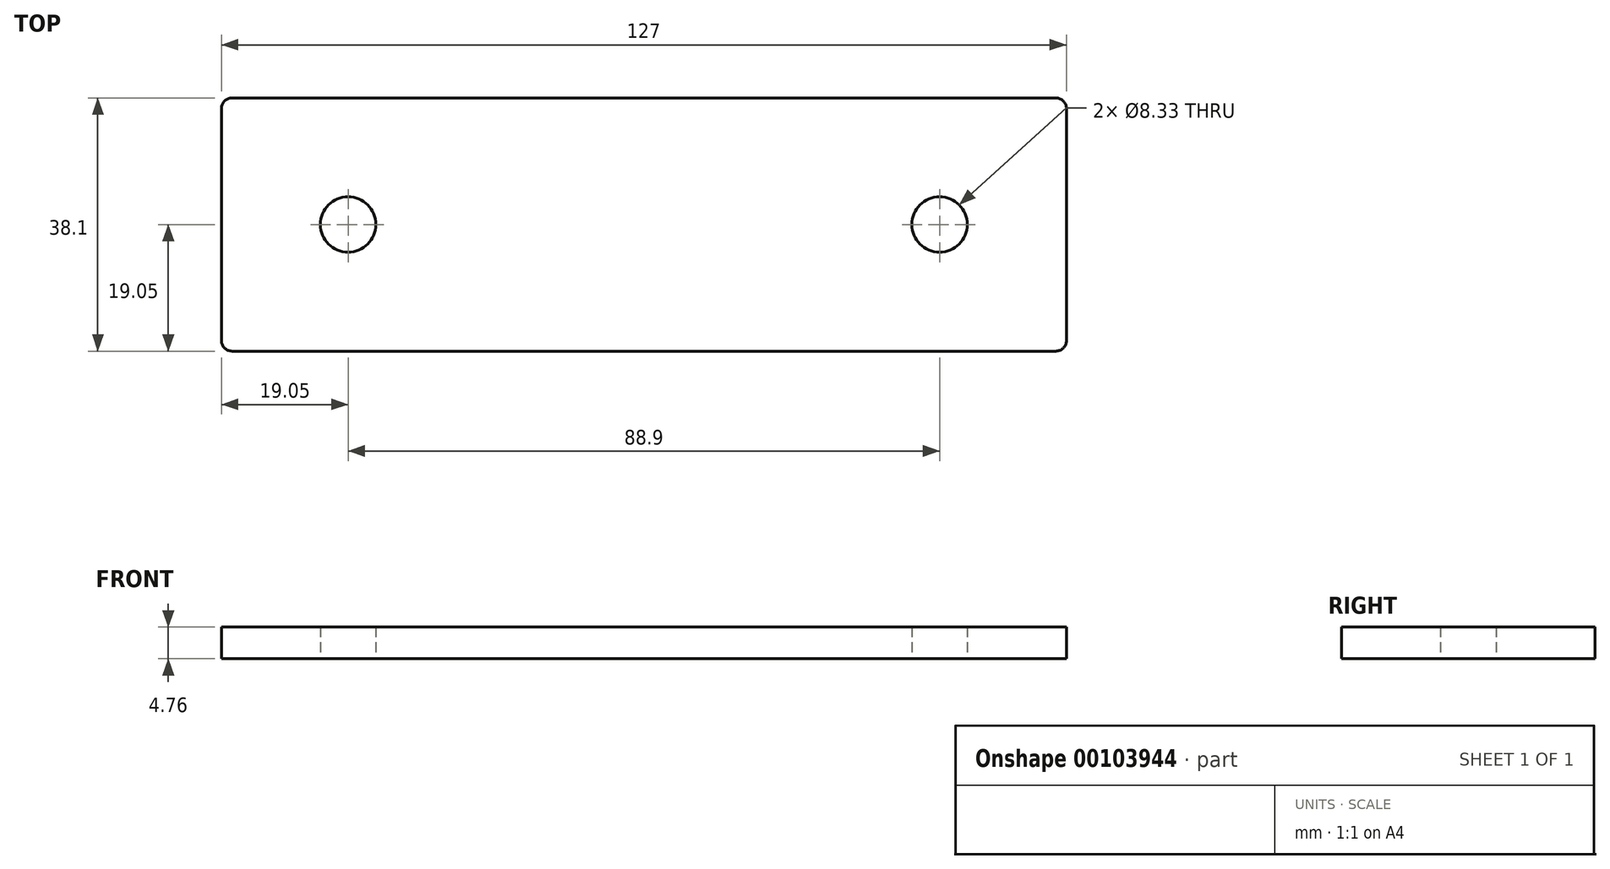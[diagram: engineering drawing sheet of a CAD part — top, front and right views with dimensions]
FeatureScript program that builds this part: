
annotation { "Feature Type Name" : "Feature", "Feature Type Description" : "" }
export const myFeature = defineFeature(function(context is Context, id is Id, definition is map)
    precondition{}
    {
        {
            var Q0;
            Q0=qCreatedBy(makeId("Top.planeOp"),FACE);
            var sketch = newSketch(context, id + "F0", { "sketchPlane" : qUnion([Q0])});
            skLineSegment(sketch, "E0.bottom", {"start": v(0, 0) * mm, "end": v(127, 0) * mm});
            skLineSegment(sketch, "E0.top", {"start": v(0, -38.1) * mm, "end": v(127, -38.1) * mm});
            skLineSegment(sketch, "E0.left", {"start": v(0, 0) * mm, "end": v(0, -38.1) * mm});
            skLineSegment(sketch, "E0.right", {"start": v(127, 0) * mm, "end": v(127, -38.1) * mm});
            skCircle(sketch, "E1", {"center": v(19.05, -19.05) * mm, "radius": 4.17 * mm});
            skCircle(sketch, "E2", {"center": v(107.95, -19.05) * mm, "radius": 4.17 * mm});
            skSolve(sketch);
        }
        {
            var Q0;
            Q0=qSketchRegion(id+"F0",true);
            extrude(context, id + "F1", {"entities" : qUnion([Q0]), "depth" : 4.76 * mm});
        }
        {
            var Q0;
            Q0=makeQuery(id+"F1.opExtrude","SWEPT_EDGE",EDGE,{"disambiguationData":[OSD([sQuery(id+"F0.wireOp",EDGE,"E0.top"),sQuery(id+"F0.wireOp",EDGE,"E0.left")])]});
            var Q1;
            Q1=makeQuery(id+"F1.opExtrude","SWEPT_EDGE",EDGE,{"disambiguationData":[OSD([sQuery(id+"F0.wireOp",EDGE,"E0.bottom"),sQuery(id+"F0.wireOp",EDGE,"E0.left")])]});
            var Q2;
            Q2=makeQuery(id+"F1.opExtrude","SWEPT_EDGE",EDGE,{"disambiguationData":[OSD([sQuery(id+"F0.wireOp",EDGE,"E0.bottom"),sQuery(id+"F0.wireOp",EDGE,"E0.right")])]});
            var Q3;
            Q3=makeQuery(id+"F1.opExtrude","SWEPT_EDGE",EDGE,{"disambiguationData":[OSD([sQuery(id+"F0.wireOp",EDGE,"E0.top"),sQuery(id+"F0.wireOp",EDGE,"E0.right")])]});
            fillet(context, id + "F2", {"entities" : qUnion([Q0, Q1, Q2, Q3]), "radius" : 1.59 * mm, "tangentPropagation" : true, "allowEdgeOverflow" : false});
        }
    });
